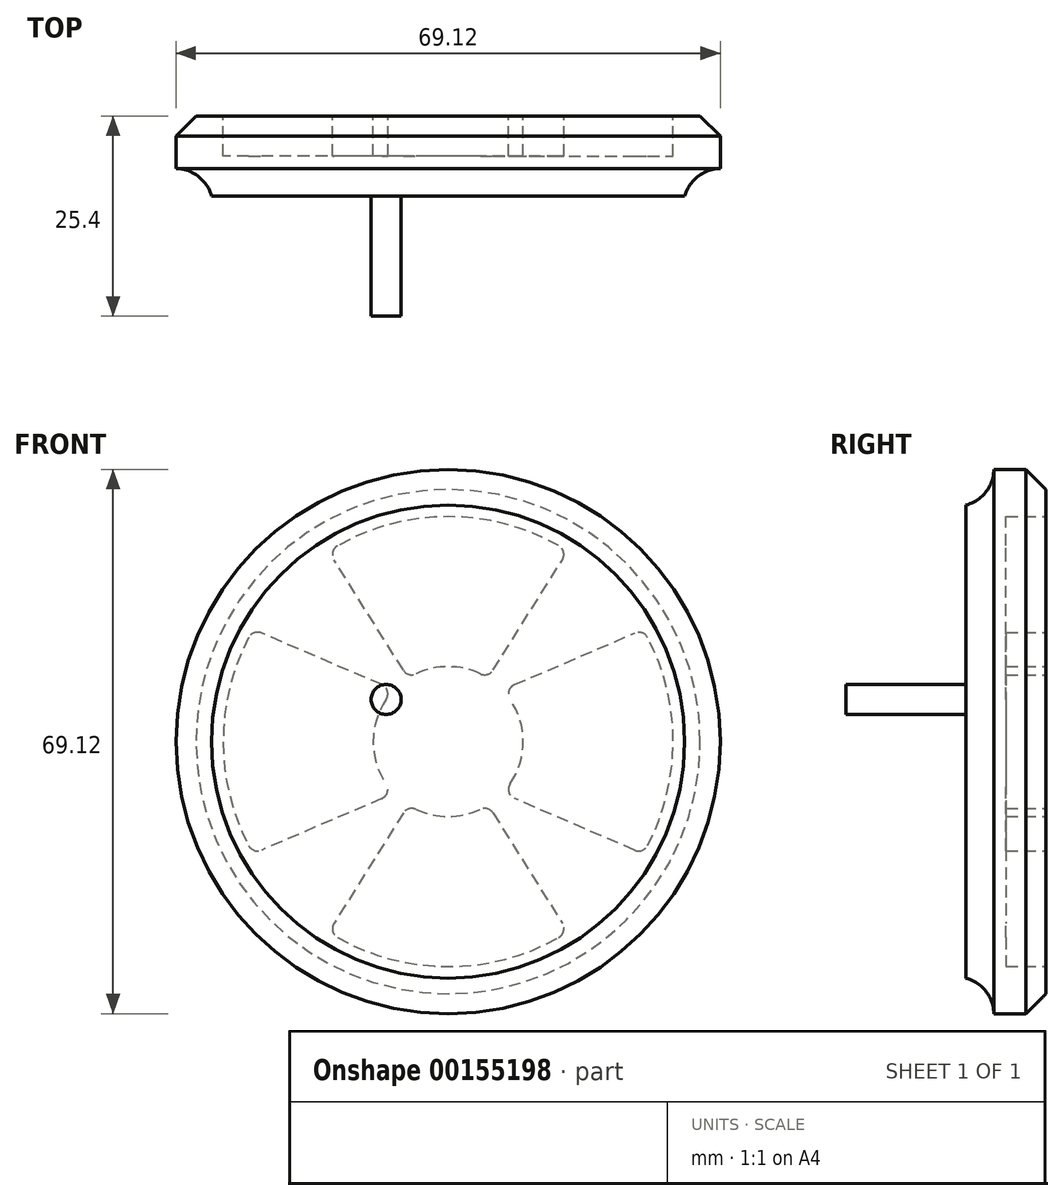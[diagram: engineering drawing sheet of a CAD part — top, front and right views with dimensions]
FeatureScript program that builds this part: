
annotation { "Feature Type Name" : "Feature", "Feature Type Description" : "" }
export const myFeature = defineFeature(function(context is Context, id is Id, definition is map)
    precondition{}
    {
        {
            var Q0;
            Q0=qCreatedBy(makeId("Front.planeOp"),FACE);
            var sketch = newSketch(context, id + "F0", { "sketchPlane" : qUnion([Q0])});
            skCircle(sketch, "E0", {"center": v(0, 0) * mm, "radius": 34.56 * mm});
            skArc(sketch, "E1", {"start": v(-7.5, 5.87) * mm, "mid": v(-9.53, 0) * mm, "end": v(-7.5, -5.87) * mm});
            skArc(sketch, "E2", {"start": v(-25.33, 13.23) * mm, "mid": v(-28.58, 0) * mm, "end": v(-25.33, -13.23) * mm});
            skLineSegment(sketch, "E3", {"start": v(-16.75, 23.15) * mm, "end": v(-5.58, 7.72) * mm});
            skLineSegment(sketch, "E4", {"start": v(0, 55.07) * mm, "end": v(0, -57.65) * mm, "construction": true});
            skLineSegment(sketch, "E5.MirrorCS", {"start": v(16.75, 23.15) * mm, "end": v(5.58, 7.72) * mm});
            skLineSegment(sketch, "E6", {"start": v(-7.5, 5.87) * mm, "end": v(-25.33, 13.23) * mm});
            skLineSegment(sketch, "E7.MirrorCS", {"start": v(7.5, 5.87) * mm, "end": v(25.33, 13.23) * mm});
            skLineSegment(sketch, "E8.MirrorCS", {"start": v(-7.5, -5.87) * mm, "end": v(-25.33, -13.23) * mm});
            skLineSegment(sketch, "E9.MirrorCS", {"start": v(7.5, -5.87) * mm, "end": v(25.33, -13.23) * mm});
            skLineSegment(sketch, "E10.MirrorCS", {"start": v(-16.75, -23.15) * mm, "end": v(-5.58, -7.72) * mm});
            skLineSegment(sketch, "E11.MirrorCS", {"start": v(16.75, -23.15) * mm, "end": v(5.58, -7.72) * mm});
            skArc(sketch, "E12.trimOffspring", {"start": v(16.75, 23.15) * mm, "mid": v(0, 28.58) * mm, "end": v(-16.75, 23.15) * mm});
            skArc(sketch, "E13.trimOffspring", {"start": v(-16.75, -23.15) * mm, "mid": v(0, -28.58) * mm, "end": v(16.75, -23.15) * mm});
            skArc(sketch, "E14.trimOffspring", {"start": v(25.33, -13.23) * mm, "mid": v(28.58, 0) * mm, "end": v(25.33, 13.23) * mm});
            skArc(sketch, "E15.trimOffspring", {"start": v(5.58, 7.72) * mm, "mid": v(0, 9.53) * mm, "end": v(-5.58, 7.72) * mm});
            skArc(sketch, "E16.trimOffspring", {"start": v(7.5, -5.87) * mm, "mid": v(9.53, 0) * mm, "end": v(7.5, 5.87) * mm});
            skArc(sketch, "E17.trimOffspring", {"start": v(-5.58, -7.72) * mm, "mid": v(0, -9.53) * mm, "end": v(5.58, -7.72) * mm});
            skSolve(sketch);
        }
        {
            var Q0;
            Q0=makeQuery(id+"F0.imprint","IMPRINT",FACE,{"disambiguationData":[TD([[makeQuery(id+"F0.imprint","IMPRINT",EDGE,{"derivedFrom":sQuery(id+"F0.wireOp",EDGE,"E0")}),1.0]])]});
            var Q1;
            Q1=makeQuery(id+"F0.imprint","IMPRINT",FACE,{"disambiguationData":[TD([[makeQuery(id+"F0.imprint","IMPRINT",EDGE,{"derivedFrom":sQuery(id+"F0.wireOp",EDGE,"E7.MirrorCS")}),-1.0]])]});
            var Q2;
            Q2=makeQuery(id+"F0.imprint","IMPRINT",FACE,{"disambiguationData":[TD([[makeQuery(id+"F0.imprint","IMPRINT",EDGE,{"derivedFrom":sQuery(id+"F0.wireOp",EDGE,"E3")}),1.0]])]});
            var Q3;
            Q3=makeQuery(id+"F0.imprint","IMPRINT",FACE,{"disambiguationData":[TD([[makeQuery(id+"F0.imprint","IMPRINT",EDGE,{"derivedFrom":sQuery(id+"F0.wireOp",EDGE,"E1")}),-1.0]])]});
            var Q4;
            Q4=makeQuery(id+"F0.imprint","IMPRINT",FACE,{"disambiguationData":[TD([[makeQuery(id+"F0.imprint","IMPRINT",EDGE,{"derivedFrom":sQuery(id+"F0.wireOp",EDGE,"E10.MirrorCS")}),-1.0]])]});
            extrude(context, id + "F1", {"entities" : qUnion([Q0, Q1, Q2, Q3, Q4]), "depth" : 25.4 * mm});
        }
        {
            var Q0;
            Q0=makeQuery(id+"F1.opExtrude","CAP_FACE",FACE,{"disambiguationData":[OSD([sQuery(id+"F0.wireOp",EDGE,"E0")])],"isStart":true});
            var sketch = newSketch(context, id + "F2", { "sketchPlane" : qUnion([Q0])});
            skArc(sketch, "E18", {"start": v(-6.9, 6.57) * mm, "mid": v(-9.53, 0) * mm, "end": v(-6.9, -6.57) * mm});
            skArc(sketch, "E19", {"start": v(-24.77, 14.25) * mm, "mid": v(-28.58, 0) * mm, "end": v(-24.77, -14.25) * mm});
            skLineSegment(sketch, "E20", {"start": v(-5.06, 8.07) * mm, "end": v(-15.2, 24.2) * mm});
            skLineSegment(sketch, "E21", {"start": v(0, 39.08) * mm, "end": v(0, -39.95) * mm, "construction": true});
            skLineSegment(sketch, "E22.MirrorCS", {"start": v(5.06, 8.07) * mm, "end": v(15.2, 24.2) * mm});
            skLineSegment(sketch, "E23", {"start": v(-6.9, 6.57) * mm, "end": v(-24.77, 14.25) * mm, "construction": true});
            skLineSegment(sketch, "E24", {"start": v(-6.9, 6.57) * mm, "end": v(-24.77, 14.25) * mm});
            skLineSegment(sketch, "E25.MirrorCS", {"start": v(6.9, 6.57) * mm, "end": v(24.77, 14.25) * mm, "construction": true});
            skLineSegment(sketch, "E26", {"start": v(6.9, 6.57) * mm, "end": v(24.77, 14.25) * mm});
            skLineSegment(sketch, "E27", {"start": v(-28.58, 0) * mm, "end": v(28.57, 0) * mm, "construction": true});
            skLineSegment(sketch, "E28.MirrorCS", {"start": v(-6.9, -6.57) * mm, "end": v(-24.77, -14.25) * mm, "construction": true});
            skLineSegment(sketch, "E29.MirrorCS", {"start": v(6.9, -6.57) * mm, "end": v(24.77, -14.25) * mm, "construction": true});
            skLineSegment(sketch, "E30.MirrorCS", {"start": v(-5.06, -8.07) * mm, "end": v(-15.2, -24.2) * mm});
            skLineSegment(sketch, "E31.MirrorCS", {"start": v(5.06, -8.07) * mm, "end": v(15.2, -24.2) * mm});
            skLineSegment(sketch, "E32", {"start": v(-24.77, -14.25) * mm, "end": v(-6.9, -6.57) * mm});
            skLineSegment(sketch, "E33", {"start": v(6.9, -6.57) * mm, "end": v(24.77, -14.25) * mm});
            skArc(sketch, "E34.trimOffspring", {"start": v(15.2, 24.2) * mm, "mid": v(0, 28.58) * mm, "end": v(-15.2, 24.2) * mm});
            skArc(sketch, "E35.trimOffspring", {"start": v(5.06, 8.07) * mm, "mid": v(0, 9.53) * mm, "end": v(-5.06, 8.07) * mm});
            skArc(sketch, "E36.trimOffspring", {"start": v(-15.2, -24.2) * mm, "mid": v(0, -28.57) * mm, "end": v(15.2, -24.2) * mm});
            skArc(sketch, "E37.trimOffspring", {"start": v(-5.06, -8.07) * mm, "mid": v(0, -9.52) * mm, "end": v(5.06, -8.07) * mm});
            skArc(sketch, "E38.trimOffspring", {"start": v(6.9, -6.57) * mm, "mid": v(9.52, 0) * mm, "end": v(6.9, 6.57) * mm});
            skArc(sketch, "E39.trimOffspring", {"start": v(24.77, -14.25) * mm, "mid": v(28.57, 0) * mm, "end": v(24.77, 14.25) * mm});
            skPoint(sketch, "E40.orphan", {"position": v(-38.48, 0) * mm});
            skSolve(sketch);
        }
        {
            var Q0;
            Q0=makeQuery(id+"F2.imprint","IMPRINT",FACE,{"disambiguationData":[TD([[makeQuery(id+"F2.imprint","IMPRINT",EDGE,{"derivedFrom":sQuery(id+"F2.wireOp",EDGE,"E18")}),-1.0]])]});
            var Q1;
            Q1=makeQuery(id+"F2.imprint","IMPRINT",FACE,{"disambiguationData":[TD([[makeQuery(id+"F2.imprint","IMPRINT",EDGE,{"derivedFrom":sQuery(id+"F2.wireOp",EDGE,"E20")}),-1.0]])]});
            var Q2;
            Q2=makeQuery(id+"F2.imprint","IMPRINT",FACE,{"disambiguationData":[TD([[makeQuery(id+"F2.imprint","IMPRINT",EDGE,{"derivedFrom":sQuery(id+"F2.wireOp",EDGE,"E26")}),-1.0]])]});
            var Q3;
            Q3=makeQuery(id+"F2.imprint","IMPRINT",FACE,{"disambiguationData":[TD([[makeQuery(id+"F2.imprint","IMPRINT",EDGE,{"derivedFrom":sQuery(id+"F2.wireOp",EDGE,"E30.MirrorCS")}),1.0]])]});
            extrude(context, id + "F3", {"entities" : qUnion([Q0, Q1, Q2, Q3]), "operationType" : NewBodyOperationType.REMOVE, "oppositeDirection" : true, "depth" : 5.08 * mm});
        }
        {
            var Q0;
            Q0=makeQuery(id+"F3.boolean.opBoolean","COPY",EDGE,{"derivedFrom":makeQuery(id+"F3.opExtrude","SWEPT_EDGE",EDGE,{"disambiguationData":[OSD([sQuery(id+"F2.wireOp",EDGE,"E19"),sQuery(id+"F2.wireOp",EDGE,"E24")])]})});
            var Q1;
            Q1=makeQuery(id+"F3.boolean.opBoolean","COPY",EDGE,{"derivedFrom":makeQuery(id+"F3.opExtrude","SWEPT_EDGE",EDGE,{"disambiguationData":[OSD([sQuery(id+"F2.wireOp",EDGE,"E19"),sQuery(id+"F2.wireOp",EDGE,"E32")])]})});
            var Q2;
            Q2=makeQuery(id+"F3.boolean.opBoolean","COPY",EDGE,{"derivedFrom":makeQuery(id+"F3.opExtrude","SWEPT_EDGE",EDGE,{"disambiguationData":[OSD([sQuery(id+"F2.wireOp",EDGE,"E18"),sQuery(id+"F2.wireOp",EDGE,"E32")])]})});
            var Q3;
            Q3=makeQuery(id+"F3.boolean.opBoolean","COPY",EDGE,{"derivedFrom":makeQuery(id+"F3.opExtrude","SWEPT_EDGE",EDGE,{"disambiguationData":[OSD([sQuery(id+"F2.wireOp",EDGE,"E18"),sQuery(id+"F2.wireOp",EDGE,"E24")])]})});
            var Q4;
            Q4=makeQuery(id+"F3.boolean.opBoolean","COPY",EDGE,{"derivedFrom":makeQuery(id+"F3.opExtrude","SWEPT_EDGE",EDGE,{"disambiguationData":[OSD([sQuery(id+"F2.wireOp",EDGE,"E20"),sQuery(id+"F2.wireOp",EDGE,"E35.trimOffspring")])]})});
            var Q5;
            Q5=makeQuery(id+"F3.boolean.opBoolean","COPY",EDGE,{"derivedFrom":makeQuery(id+"F3.opExtrude","SWEPT_EDGE",EDGE,{"disambiguationData":[OSD([sQuery(id+"F2.wireOp",EDGE,"E20"),sQuery(id+"F2.wireOp",EDGE,"E34.trimOffspring")])]})});
            var Q6;
            Q6=makeQuery(id+"F3.boolean.opBoolean","COPY",EDGE,{"derivedFrom":makeQuery(id+"F3.opExtrude","SWEPT_EDGE",EDGE,{"disambiguationData":[OSD([sQuery(id+"F2.wireOp",EDGE,"E22.MirrorCS"),sQuery(id+"F2.wireOp",EDGE,"E34.trimOffspring")])]})});
            var Q7;
            Q7=makeQuery(id+"F3.boolean.opBoolean","COPY",EDGE,{"derivedFrom":makeQuery(id+"F3.opExtrude","SWEPT_EDGE",EDGE,{"disambiguationData":[OSD([sQuery(id+"F2.wireOp",EDGE,"E22.MirrorCS"),sQuery(id+"F2.wireOp",EDGE,"E35.trimOffspring")])]})});
            var Q8;
            Q8=makeQuery(id+"F3.boolean.opBoolean","COPY",EDGE,{"derivedFrom":makeQuery(id+"F3.opExtrude","SWEPT_EDGE",EDGE,{"disambiguationData":[OSD([sQuery(id+"F2.wireOp",EDGE,"E26"),sQuery(id+"F2.wireOp",EDGE,"E38.trimOffspring")])]})});
            var Q9;
            Q9=makeQuery(id+"F3.boolean.opBoolean","COPY",EDGE,{"derivedFrom":makeQuery(id+"F3.opExtrude","SWEPT_EDGE",EDGE,{"disambiguationData":[OSD([sQuery(id+"F2.wireOp",EDGE,"E33"),sQuery(id+"F2.wireOp",EDGE,"E38.trimOffspring")])]})});
            var Q10;
            Q10=makeQuery(id+"F3.boolean.opBoolean","COPY",EDGE,{"derivedFrom":makeQuery(id+"F3.opExtrude","SWEPT_EDGE",EDGE,{"disambiguationData":[OSD([sQuery(id+"F2.wireOp",EDGE,"E33"),sQuery(id+"F2.wireOp",EDGE,"E39.trimOffspring")])]})});
            var Q11;
            Q11=makeQuery(id+"F3.boolean.opBoolean","COPY",EDGE,{"derivedFrom":makeQuery(id+"F3.opExtrude","SWEPT_EDGE",EDGE,{"disambiguationData":[OSD([sQuery(id+"F2.wireOp",EDGE,"E26"),sQuery(id+"F2.wireOp",EDGE,"E39.trimOffspring")])]})});
            var Q12;
            Q12=makeQuery(id+"F3.boolean.opBoolean","COPY",EDGE,{"derivedFrom":makeQuery(id+"F3.opExtrude","SWEPT_EDGE",EDGE,{"disambiguationData":[OSD([sQuery(id+"F2.wireOp",EDGE,"E31.MirrorCS"),sQuery(id+"F2.wireOp",EDGE,"E37.trimOffspring")])]})});
            var Q13;
            Q13=makeQuery(id+"F3.boolean.opBoolean","COPY",EDGE,{"derivedFrom":makeQuery(id+"F3.opExtrude","SWEPT_EDGE",EDGE,{"disambiguationData":[OSD([sQuery(id+"F2.wireOp",EDGE,"E30.MirrorCS"),sQuery(id+"F2.wireOp",EDGE,"E37.trimOffspring")])]})});
            var Q14;
            Q14=makeQuery(id+"F3.boolean.opBoolean","COPY",EDGE,{"derivedFrom":makeQuery(id+"F3.opExtrude","SWEPT_EDGE",EDGE,{"disambiguationData":[OSD([sQuery(id+"F2.wireOp",EDGE,"E30.MirrorCS"),sQuery(id+"F2.wireOp",EDGE,"E36.trimOffspring")])]})});
            var Q15;
            Q15=makeQuery(id+"F3.boolean.opBoolean","COPY",EDGE,{"derivedFrom":makeQuery(id+"F3.opExtrude","SWEPT_EDGE",EDGE,{"disambiguationData":[OSD([sQuery(id+"F2.wireOp",EDGE,"E31.MirrorCS"),sQuery(id+"F2.wireOp",EDGE,"E36.trimOffspring")])]})});
            fillet(context, id + "F4", {"entities" : qUnion([Q0, Q1, Q2, Q3, Q4, Q5, Q6, Q7, Q8, Q9, Q10, Q11, Q12, Q13, Q14, Q15]), "radius" : 1.27 * mm, "tangentPropagation" : true, "allowEdgeOverflow" : false});
        }
        {
            var Q0;
            Q0=qCreatedBy(makeId("Top.planeOp"),FACE);
            var sketch = newSketch(context, id + "F5", { "sketchPlane" : qUnion([Q0])});
            skCircle(sketch, "E41", {"center": v(34.66, -11.43) * mm, "radius": 4.79 * mm});
            skSolve(sketch);
        }
        {
            var Q0;
            Q0=makeQuery(id+"F5.imprint","IMPRINT",FACE,{"disambiguationData":[TD([[makeQuery(id+"F5.imprint","IMPRINT",EDGE,{"derivedFrom":sQuery(id+"F5.wireOp",EDGE,"E41")}),1.0]])]});
            var Q1;
            Q1=makeQuery(id+"F1.opExtrude","SWEPT_FACE",FACE,{"disambiguationData":[OSD([sQuery(id+"F0.wireOp",EDGE,"E0")])]});
            revolve(context, id + "F6", {"operationType" : NewBodyOperationType.REMOVE, "entities" : qUnion([Q0]), "axis" : qUnion([Q1]), "revolveType" : RevolveType.FULL, "oppositeDirection" : true});
        }
        {
            var Q0;
            Q0=makeQuery(id+"F1.opExtrude","CAP_EDGE",EDGE,{"disambiguationData":[OSD([sQuery(id+"F0.wireOp",EDGE,"E0")])],"isStart":true});
            chamfer(context, id + "F7", {"entities" : qUnion([Q0]), "width" : 2.54 * mm, "tangentPropagation" : true});
        }
        {
            var Q0;
            Q0=makeQuery(id+"F1.opExtrude","CAP_FACE",FACE,{"disambiguationData":[OSD([sQuery(id+"F0.wireOp",EDGE,"E0")])],"isStart":false});
            var sketch = newSketch(context, id + "F8", { "sketchPlane" : qUnion([Q0])});
            skCircle(sketch, "E42", {"center": v(7.88, 5.35) * mm, "radius": 1.9 * mm});
            skCircle(sketch, "E43", {"center": v(0, -9.52) * mm, "radius": 1.9 * mm});
            skCircle(sketch, "E44.MirrorC", {"center": v(-7.88, 5.35) * mm, "radius": 1.9 * mm});
            skSolve(sketch);
        }
        {
            var Q0;
            Q0=makeQuery(id+"F8.imprint","IMPRINT",FACE,{"disambiguationData":[TD([[makeQuery(id+"F8.imprint","IMPRINT",EDGE,{"derivedFrom":sQuery(id+"F8.wireOp",EDGE,"E44.MirrorC")}),-1.0]])]});
            var Q1;
            Q1=makeQuery(id+"F8.imprint","IMPRINT",FACE,{"disambiguationData":[TD([[makeQuery(id+"F8.imprint","IMPRINT",EDGE,{"derivedFrom":sQuery(id+"F8.wireOp",EDGE,"E42")}),1.0]])]});
            var Q2;
            Q2=makeQuery(id+"F8.imprint","IMPRINT",FACE,{"disambiguationData":[TD([[makeQuery(id+"F8.imprint","IMPRINT",EDGE,{"derivedFrom":sQuery(id+"F8.wireOp",EDGE,"E43")}),1.0]])]});
            extrude(context, id + "F9", {"entities" : qUnion([Q0, Q1, Q2]), "operationType" : NewBodyOperationType.REMOVE, "oppositeDirection" : true, "depth" : 15.24 * mm});
        }
    });
